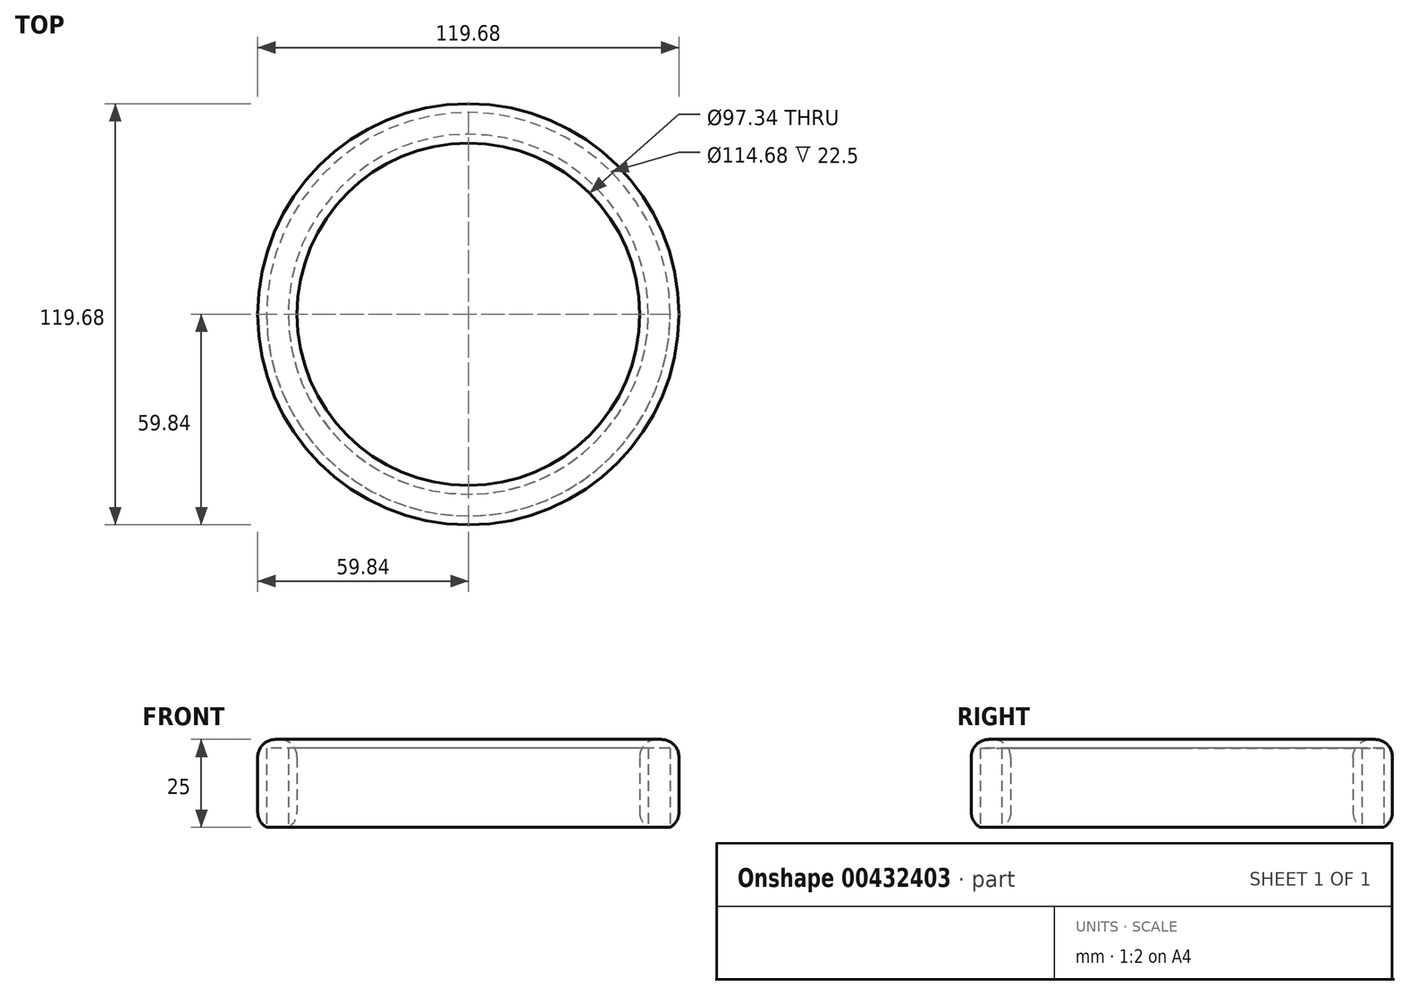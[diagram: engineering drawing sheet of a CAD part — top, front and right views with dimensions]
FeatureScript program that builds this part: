
annotation { "Feature Type Name" : "Feature", "Feature Type Description" : "" }
export const myFeature = defineFeature(function(context is Context, id is Id, definition is map)
    precondition{}
    {
        {
            var Q0;
            Q0=qCreatedBy(makeId("Top.planeOp"),FACE);
            var sketch = newSketch(context, id + "F0", { "sketchPlane" : qUnion([Q0])});
            skCircle(sketch, "E0", {"center": v(0, 0) * mm, "radius": 59.84 * mm});
            skCircle(sketch, "E1", {"center": v(0, 0) * mm, "radius": 48.67 * mm});
            skSolve(sketch);
        }
        {
            var Q0;
            Q0=qCreatedBy(makeId("Top.planeOp"),FACE);
            var sketch = newSketch(context, id + "F1", { "sketchPlane" : qUnion([Q0])});
            skLineSegment(sketch, "E2", {"start": v(0, 130.12) * mm, "end": v(0, -107.14) * mm});
            skLineSegment(sketch, "E3", {"start": v(0, -107.14) * mm, "end": v(0, 0) * mm});
            skLineSegment(sketch, "E4", {"start": v(0, 0) * mm, "end": v(96.48, 0) * mm});
            skLineSegment(sketch, "E5", {"start": v(96.48, 0) * mm, "end": v(-103.62, 0) * mm});
            skLineSegment(sketch, "E6", {"start": v(-103.62, 0) * mm, "end": v(0, 0) * mm});
            skSolve(sketch);
        }
        {
            var Q0;
            Q0=qCreatedBy(makeId("Top.planeOp"),FACE);
            var sketch = newSketch(context, id + "F2", { "sketchPlane" : qUnion([Q0])});
            skLineSegment(sketch, "E7", {"start": v(-73.74, 74.46) * mm, "end": v(74.41, -73.8) * mm});
            skLineSegment(sketch, "E8", {"start": v(0, 0) * mm, "end": v(73.24, 72.65) * mm});
            skLineSegment(sketch, "E9", {"start": v(73.24, 72.65) * mm, "end": v(-74.92, -75.4) * mm});
            skSolve(sketch);
        }
        {
            var Q0;
            Q0=makeQuery(id+"F0.imprint","IMPRINT",FACE,{"disambiguationData":[TD([[makeQuery(id+"F0.imprint","IMPRINT",EDGE,{"derivedFrom":sQuery(id+"F0.wireOp",EDGE,"E0")}),1.0]])]});
            extrude(context, id + "F3", {"entities" : qUnion([Q0]), "depth" : 25 * mm});
        }
        {
            var Q0;
            Q0=sQuery(id+"F1.wireOp",EDGE,"E2");
            extrude(context, id + "F4", {"bodyType" : ToolBodyType.SURFACE, "surfaceEntities" : qUnion([Q0]), "depth" : 25 * mm});
        }
        {
            var Q0;
            Q0=sQuery(id+"F2.wireOp",EDGE,"E7");
            extrude(context, id + "F5", {"bodyType" : ToolBodyType.SURFACE, "surfaceEntities" : qUnion([Q0]), "depth" : 25 * mm});
        }
        {
            var Q0;
            Q0=sQuery(id+"F1.wireOp",EDGE,"E5");
            extrude(context, id + "F6", {"bodyType" : ToolBodyType.SURFACE, "surfaceEntities" : qUnion([Q0]), "depth" : 25 * mm});
        }
        {
            var Q0;
            Q0=makeQuery(id+"F3.opExtrude","CAP_FACE",FACE,{"disambiguationData":[OSD([sQuery(id+"F0.wireOp",EDGE,"E0"),sQuery(id+"F0.wireOp",EDGE,"E1")])],"isStart":true});
            shell(context, id + "F7", {"entities" : qUnion([Q0]), "thickness" : 2.5 * mm});
        }
        {
            var Q0;
            Q0=makeQuery(id+"F3.opExtrude","SWEPT_FACE",FACE,{"disambiguationData":[OSD([sQuery(id+"F0.wireOp",EDGE,"E0")])]});
            fillet(context, id + "F8", {"entities" : qUnion([Q0]), "radius" : 5 * mm, "tangentPropagation" : true, "allowEdgeOverflow" : false});
        }
        {
            var Q0;
            Q0=makeQuery(id+"F3.opExtrude","SWEPT_FACE",FACE,{"disambiguationData":[OSD([sQuery(id+"F0.wireOp",EDGE,"E1")])]});
            fillet(context, id + "F9", {"entities" : qUnion([Q0]), "radius" : 5 * mm, "tangentPropagation" : true, "allowEdgeOverflow" : false});
        }
    });
